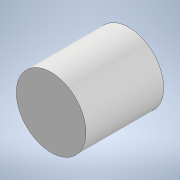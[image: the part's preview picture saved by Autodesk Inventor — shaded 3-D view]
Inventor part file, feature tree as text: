
AUTODESK INVENTOR PART (.ipt)
format: ipt  version: 2022.3 (Build 263350000, 350)  size: 90,112 bytes
history: native  units: mm
features: extrude x1, sketch x1
ambient origin geometry x8: Origin, YZ Plane, XZ Plane, XY Plane, X Axis, Y Axis, Z Axis, Center Point
bodies: Solid1 (feature_tree)
feature tree (2):
  extrude  "Extrusion1"  [1 undecoded]
  sketch  "Sketch1"  dims[d0=2.5mm d1=0.0mm]
note: 1 required parameter value undecoded (feature->parameter linkage not recoverable at this tier; creation-order binding heuristic only, values carry confidence <= 0.55)
